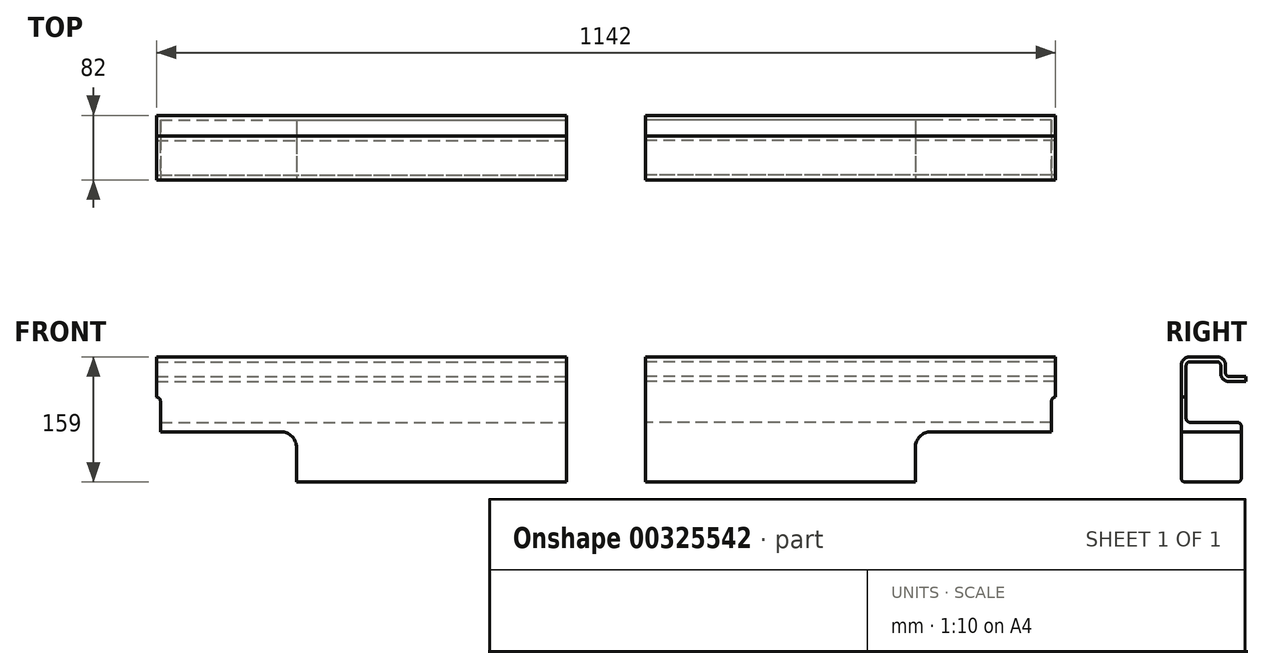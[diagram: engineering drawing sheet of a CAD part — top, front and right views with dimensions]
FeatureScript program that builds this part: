
annotation { "Feature Type Name" : "Feature", "Feature Type Description" : "" }
export const myFeature = defineFeature(function(context is Context, id is Id, definition is map)
    precondition{}
    {
        {
            var Q0;
            Q0=qCreatedBy(makeId("Right.planeOp"),FACE);
            var sketch = newSketch(context, id + "F0", { "sketchPlane" : qUnion([Q0])});
            skLineSegment(sketch, "E0", {"start": v(35.66, 132.22) * mm, "end": v(14.66, 132.22) * mm});
            skLineSegment(sketch, "E1", {"start": v(9.66, 137.22) * mm, "end": v(9.66, 147.22) * mm});
            skLineSegment(sketch, "E2", {"start": v(-0.34, 157.22) * mm, "end": v(-36.34, 157.22) * mm});
            skLineSegment(sketch, "E3", {"start": v(-46.34, 147.22) * mm, "end": v(-46.34, 3.22) * mm});
            skLineSegment(sketch, "E4", {"start": v(-41.34, -1.78) * mm, "end": v(24.66, -1.78) * mm});
            skLineSegment(sketch, "E5", {"start": v(29.66, 3.22) * mm, "end": v(29.66, 69.22) * mm});
            skLineSegment(sketch, "E6", {"start": v(24.66, 74.22) * mm, "end": v(-35.34, 74.22) * mm});
            skLineSegment(sketch, "E7", {"start": v(-40.34, 79.22) * mm, "end": v(-40.34, 146.22) * mm});
            skLineSegment(sketch, "E8", {"start": v(-35.34, 151.22) * mm, "end": v(-1.34, 151.22) * mm});
            skLineSegment(sketch, "E9", {"start": v(3.66, 146.22) * mm, "end": v(3.66, 136.22) * mm});
            skLineSegment(sketch, "E10", {"start": v(13.66, 126.22) * mm, "end": v(35.66, 126.22) * mm});
            skLineSegment(sketch, "E11", {"start": v(35.66, 126.22) * mm, "end": v(35.66, 132.22) * mm});
            skPoint(sketch, "E12.visualSharp", {"position": v(-40.34, 151.22) * mm});
            skArc(sketch, "E12.filletArc", {"start": v(-35.34, 151.22) * mm, "mid": v(-38.87, 149.75) * mm, "end": v(-40.34, 146.22) * mm});
            skPoint(sketch, "E13.visualSharp", {"position": v(3.66, 151.22) * mm});
            skArc(sketch, "E13.filletArc", {"start": v(3.66, 146.22) * mm, "mid": v(2.2, 149.75) * mm, "end": v(-1.34, 151.22) * mm});
            skPoint(sketch, "E14.visualSharp", {"position": v(9.66, 132.22) * mm});
            skArc(sketch, "E14.filletArc", {"start": v(9.66, 137.22) * mm, "mid": v(11.13, 133.68) * mm, "end": v(14.66, 132.22) * mm});
            skPoint(sketch, "E15.visualSharp", {"position": v(-40.34, 74.22) * mm});
            skArc(sketch, "E15.filletArc", {"start": v(-40.34, 79.22) * mm, "mid": v(-38.87, 75.68) * mm, "end": v(-35.34, 74.22) * mm});
            skPoint(sketch, "E16.visualSharp", {"position": v(29.66, 74.22) * mm});
            skArc(sketch, "E16.filletArc", {"start": v(29.66, 69.22) * mm, "mid": v(28.2, 72.75) * mm, "end": v(24.66, 74.22) * mm});
            skPoint(sketch, "E17.visualSharp", {"position": v(29.66, -1.78) * mm});
            skArc(sketch, "E17.filletArc", {"start": v(24.66, -1.78) * mm, "mid": v(28.2, -0.32) * mm, "end": v(29.66, 3.22) * mm});
            skPoint(sketch, "E18.visualSharp", {"position": v(-46.34, -1.78) * mm});
            skArc(sketch, "E18.filletArc", {"start": v(-46.34, 3.22) * mm, "mid": v(-44.87, -0.32) * mm, "end": v(-41.34, -1.78) * mm});
            skPoint(sketch, "E19.visualSharp", {"position": v(-46.34, 157.22) * mm});
            skArc(sketch, "E19.filletArc", {"start": v(-36.34, 157.22) * mm, "mid": v(-43.4, 154.29) * mm, "end": v(-46.34, 147.22) * mm});
            skPoint(sketch, "E20.visualSharp", {"position": v(9.66, 157.22) * mm});
            skArc(sketch, "E20.filletArc", {"start": v(9.66, 147.22) * mm, "mid": v(6.73, 154.29) * mm, "end": v(-0.34, 157.22) * mm});
            skPoint(sketch, "E21.visualSharp", {"position": v(3.66, 126.22) * mm});
            skArc(sketch, "E21.filletArc", {"start": v(3.66, 136.22) * mm, "mid": v(6.6, 129.15) * mm, "end": v(13.66, 126.22) * mm});
            skSolve(sketch);
        }
        {
            var Q0;
            Q0=makeQuery(id+"F0.imprint","IMPRINT",FACE,{"disambiguationData":[TD([[makeQuery(id+"F0.imprint","IMPRINT",EDGE,{"derivedFrom":sQuery(id+"F0.wireOp",EDGE,"E0")}),1.0]])]});
            extrude(context, id + "F1", {"entities" : qUnion([Q0]), "depth" : 521 * mm});
        }
        {
            var Q0;
            Q0=makeQuery(id+"F1.opExtrude","SWEPT_FACE",FACE,{"disambiguationData":[OSD([sQuery(id+"F0.wireOp",EDGE,"E3")])]});
            var sketch = newSketch(context, id + "F2", { "sketchPlane" : qUnion([Q0])});
            skLineSegment(sketch, "E22", {"start": v(521, 106.22) * mm, "end": v(521, 106.22) * mm});
            skLineSegment(sketch, "E23", {"start": v(516, 101.22) * mm, "end": v(516, 62.22) * mm});
            skLineSegment(sketch, "E24", {"start": v(516, 62.22) * mm, "end": v(363, 62.22) * mm});
            skLineSegment(sketch, "E25", {"start": v(343, 42.22) * mm, "end": v(343, -10.7) * mm});
            skLineSegment(sketch, "E26", {"start": v(343, -10.7) * mm, "end": v(521, -10.7) * mm});
            skLineSegment(sketch, "E27", {"start": v(521, -10.7) * mm, "end": v(521, 106.22) * mm});
            skPoint(sketch, "E28.visualSharp", {"position": v(516, 106.22) * mm});
            skArc(sketch, "E28.filletArc", {"start": v(521, 106.22) * mm, "mid": v(517.46, 104.75) * mm, "end": v(516, 101.22) * mm});
            skPoint(sketch, "E29.visualSharp", {"position": v(343, 62.22) * mm});
            skArc(sketch, "E29.filletArc", {"start": v(363, 62.22) * mm, "mid": v(348.86, 56.36) * mm, "end": v(343, 42.22) * mm});
            skSolve(sketch);
        }
        {
            var Q0;
            Q0=makeQuery(id+"F2.imprint","IMPRINT",FACE,{"disambiguationData":[TD([[makeQuery(id+"F2.imprint","IMPRINT",EDGE,{"derivedFrom":sQuery(id+"F2.wireOp",EDGE,"E23")}),1.0]])]});
            var Q1;
            {var subQ0=sQuery(id+"F2.wireOp",EDGE,"E26");Q1=makeQuery(id+"F2.imprint","IMPRINT",FACE,{"disambiguationData":[TD([[makeQuery(id+"F2.imprint","IMPRINT",EDGE,{"derivedFrom":subQ0}),1.0]])]});}
            extrude(context, id + "F3", {"entities" : qUnion([Q0, Q1]), "operationType" : NewBodyOperationType.REMOVE, "oppositeDirection" : true, "depth" : 76 * mm});
        }
        {
            var Q0;
            Q0=qCreatedBy(makeId("Right.planeOp"),FACE);
            cPlane(context, id + "F4", {"entities" : qUnion([Q0]), "cplaneType" : CPlaneType.OFFSET, "offset" : 50 * mm, "oppositeDirection" : true, "width" : 150 * mm, "height" : 150 * mm});
        }
        {
            var Q0;
            Q0=makeQuery(id+"F1.opExtrude","SWEPT_BODY",BODY,{"disambiguationData":[OSD([sQuery(id+"F0.wireOp",EDGE,"E0"),sQuery(id+"F0.wireOp",EDGE,"E1"),sQuery(id+"F0.wireOp",EDGE,"E2"),sQuery(id+"F0.wireOp",EDGE,"E3"),sQuery(id+"F0.wireOp",EDGE,"E4"),sQuery(id+"F0.wireOp",EDGE,"E5"),sQuery(id+"F0.wireOp",EDGE,"E6"),sQuery(id+"F0.wireOp",EDGE,"E7"),sQuery(id+"F0.wireOp",EDGE,"E8"),sQuery(id+"F0.wireOp",EDGE,"E9"),sQuery(id+"F0.wireOp",EDGE,"E10"),sQuery(id+"F0.wireOp",EDGE,"E11"),sQuery(id+"F0.wireOp",EDGE,"E12.filletArc"),sQuery(id+"F0.wireOp",EDGE,"E13.filletArc"),sQuery(id+"F0.wireOp",EDGE,"E14.filletArc"),sQuery(id+"F0.wireOp",EDGE,"E15.filletArc"),sQuery(id+"F0.wireOp",EDGE,"E16.filletArc"),sQuery(id+"F0.wireOp",EDGE,"E17.filletArc"),sQuery(id+"F0.wireOp",EDGE,"E18.filletArc"),sQuery(id+"F0.wireOp",EDGE,"E19.filletArc"),sQuery(id+"F0.wireOp",EDGE,"E20.filletArc"),sQuery(id+"F0.wireOp",EDGE,"E21.filletArc")])]});
            var Q1;
            Q1=qCreatedBy(id+"F4.planeOp",FACE);
            mirror(context, id + "F5", {"entities" : qUnion([Q0]), "mirrorPlane" : qUnion([Q1])});
        }
    });
